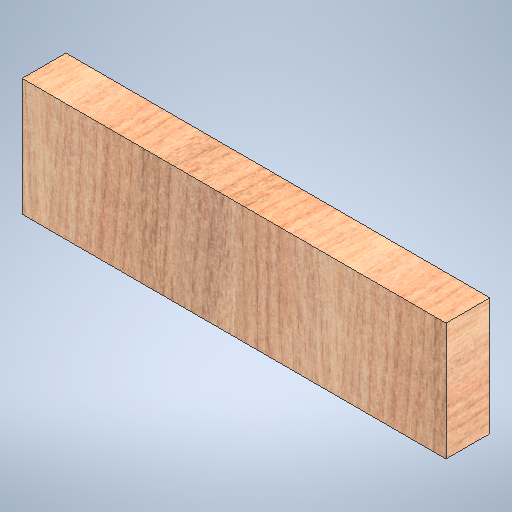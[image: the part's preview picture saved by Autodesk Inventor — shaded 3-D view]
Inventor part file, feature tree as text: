
AUTODESK INVENTOR PART (.ipt)
format: ipt  version: 2025.1 (Build 291241020, 241B)  size: 423,936 bytes
history: native  units: in
note: dims shown in document units (in); Inventor stores cm internally (conversion verified against a paired STEP export)
features: extrude x1, sketch x1
ambient origin geometry x8: Origin, YZ Plane, XZ Plane, XY Plane, X Axis, Y Axis, Z Axis, Center Point
bodies: Solid1 (feature_tree)
feature tree (2):
  extrude  "Extrusion1"  Depth=14.5in
  sketch  "Sketch1"  dims[d2=4.023in d3=14.5in d4=1.5in d5=0.0in]
